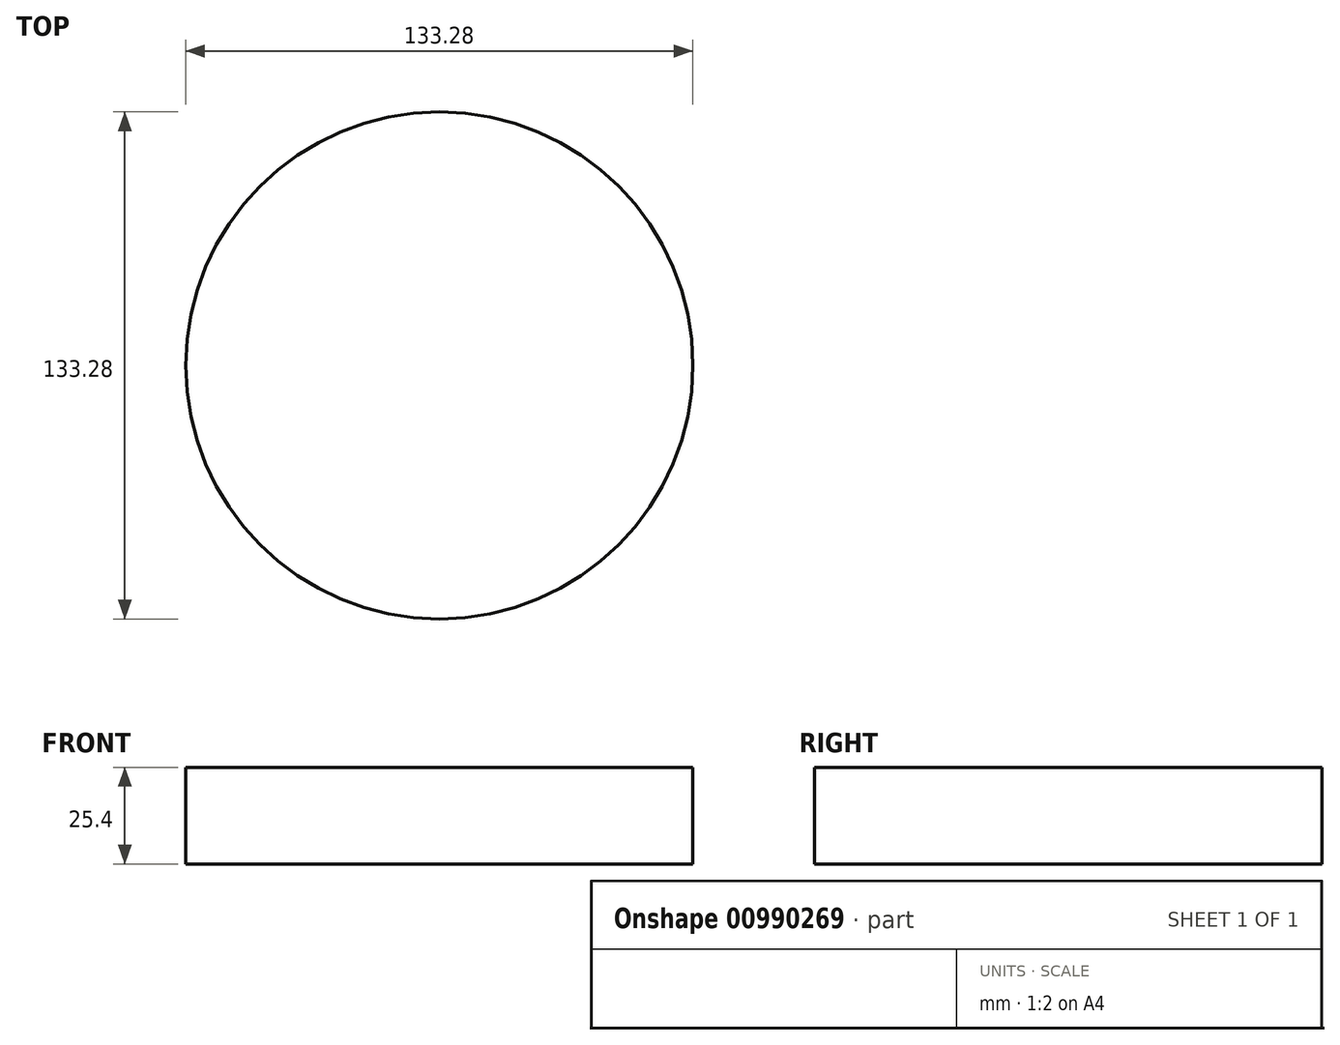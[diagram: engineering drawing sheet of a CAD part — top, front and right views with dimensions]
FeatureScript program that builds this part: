
annotation { "Feature Type Name" : "Feature", "Feature Type Description" : "" }
export const myFeature = defineFeature(function(context is Context, id is Id, definition is map)
    precondition{}
    {
        {
            var Q0;
            Q0=qCreatedBy(makeId("Top.planeOp"),FACE);
            var sketch = newSketch(context, id + "F0", { "sketchPlane" : qUnion([Q0])});
            skCircle(sketch, "E0", {"center": v(0, 0) * mm, "radius": 66.64 * mm});
            skSolve(sketch);
        }
        {
            var Q0;
            Q0=makeQuery(id+"F0.imprint","IMPRINT",FACE,{"disambiguationData":[TD([[makeQuery(id+"F0.imprint","IMPRINT",EDGE,{"derivedFrom":sQuery(id+"F0.wireOp",EDGE,"E0")}),1.0]])]});
            extrude(context, id + "F1", {"entities" : qUnion([Q0]), "depth" : 25.4 * mm, "offsetDistance" : 25.4 * mm});
        }
    });
